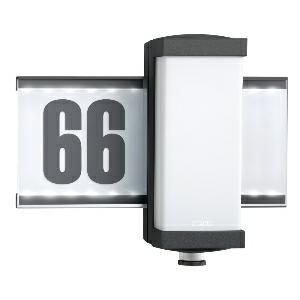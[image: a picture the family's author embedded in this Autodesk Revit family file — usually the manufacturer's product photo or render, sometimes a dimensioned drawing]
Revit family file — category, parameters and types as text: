
# Revit family: l_665_led_053949
name_source: partatom
category: Leuchten
revit_build: Autodesk Revit 2016 (Build: 20190508_0715(x64)
units: mm (PartAtom-declared; Revit-internal decimal feet)

## family parameters
Basisbauteil = Fläche
Beim Laden mit Abzugskörper schneiden = Nein
Bemaßung runder Anschluss = Durchmesser verwenden
Gemeinsam genutzt = Nein
Lichtquelle = Nein
Raumberechnungspunkt = Nein
Teiletyp = Normal

## types (1)
- L 665 LED (1 x , 655 lm, 3000 K)
    Beschreibung = Dimensions (L x W x H): 122 x 326 x 269 mm; Mains power supply: 220 – 240 V / 50 – 60 Hz; Mounting height max.: 2,50 m; Sensor Technology: passive infrared; Output: 10 W; Output, detail: 1 W LED house number illumination; Interconnection: Yes; Slave modeselectable: No; Luminous flux: 655 lm; Efficiency: 65 lm/W; Colour temperature: 3000 K; Colour variation LED: SDCM3; Colour Rendering Index CRI: 80-89; With lamp: Yes, STEINEL LED system; Lamp: LED cannot be replaced; LED life expectancy (max. °C): 50000 h; Base: without; LED cooling system: Passive Thermo Control; With motion detector: Yes; Detection angle: 360 °; Sneak-by guard: Yes; Capability of masking out individual segments: Yes; Electronic scalability: No; Mechanical scalability: No; Reach, radial: r = 2 m (13 m²); Reach, tangential: r = 7 m (154 m²); Photo-cell controller: Yes; Twilight setting: 2 – 1000 lx; Time setting: 5 sec – 15 min; Basic light level function: Yes; Basic light level function time: 10/30 min, all night; Functions: 4 programme settings geared to practical needs, can be selected on removable sensor module; Soft light start: Yes; Continuous light: selectable, 4h; Impact resistance: IK07; IP-rating: IP44; Protection class: I; Ambient temperature: -20 – 50 °C; Housing material: Aluminium; Cover material: Plastic, opal; Manufacturer's Warranty: 5 years; includes sheet of self-adhesive numbers: Yes; Settings via: Potentiometers; Cover material: shrouds; Version: Anthracite; PU1, EAN: 4007841053949
    CIE Flux Codes = 39 68 89 84 100
    Color Rendering = 80-89
    Color Temperature = 3000 K
    Frequency = 50 Hz, 60 Hz
    Height = 269 mm
    Hersteller = Steinel
    Lamp Light Flux = 655 lm
    Lamp count = 1
    Lampe = 1 x
    Length = 122 mm
    Luminous efficacy = 66 lm/W
    ModVariant = Nein
    Modell = 053949
    Mounting Type = Surface mounted
    Number of Poles = 1
    OnlyDefault = Ja
    Power Factor = 1
    Product Name = L 665 LED
    Product group = Sensor-switched indoor light
    ProductGroupID = 30
    Protection Class = Protection class I
    Protection Degree = IP 34
    RlxData = <blob elided: 40465 chars, md5=824bad6c>
    Scheinlast = 10 VA
    Socket = socket
    Standby Power = 0 W
    System Light Flux = 655 lm
    System Power = 10 W
    Typenbild = produkt1_053949.jpg
    Typenkommentare = Product without accessories
    URL = http://relux.com
    VarID = ---
    Voltage = 0 V
    Vorgabe-Ansicht = 1800 mm
    Weight = 0.00 kg
    Width = 326 mm

## geometry (parser evidence)
native form markers: Sweep x10
no freeform markers — native parametric forms only
